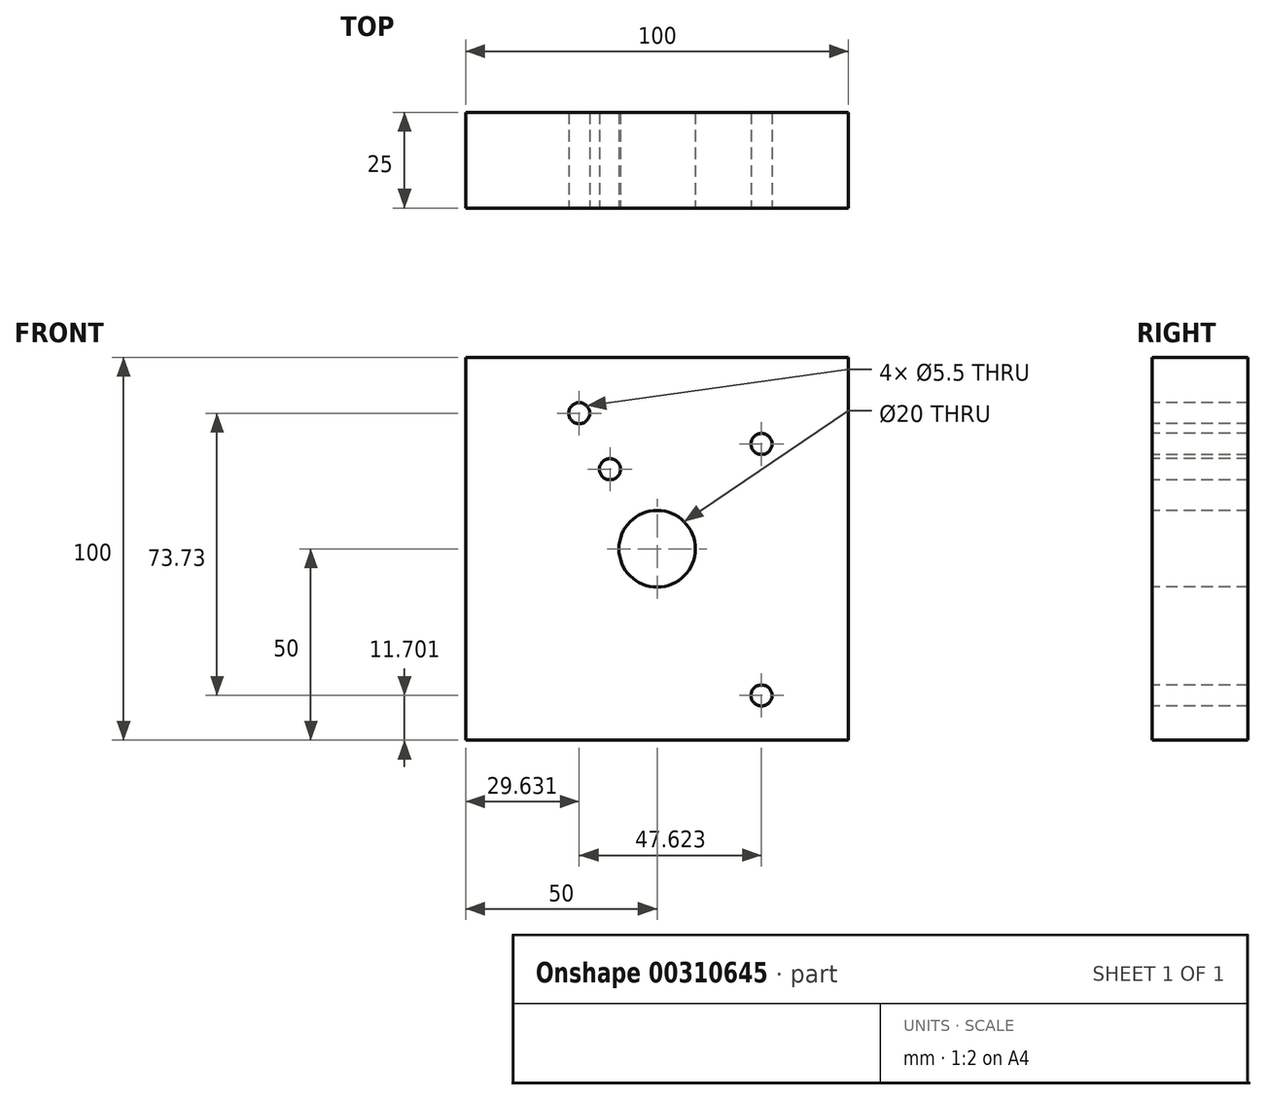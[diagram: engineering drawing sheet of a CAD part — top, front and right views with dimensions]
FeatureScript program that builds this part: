
annotation { "Feature Type Name" : "Feature", "Feature Type Description" : "" }
export const myFeature = defineFeature(function(context is Context, id is Id, definition is map)
    precondition{}
    {
        {
            var Q0;
            Q0=qCreatedBy(makeId("Front.planeOp"),FACE);
            var sketch = newSketch(context, id + "F0", { "sketchPlane" : qUnion([Q0])});
            skLineSegment(sketch, "E0.bottom", {"start": v(-50, 50) * mm, "end": v(50, 50) * mm});
            skLineSegment(sketch, "E0.top", {"start": v(-50, -50) * mm, "end": v(50, -50) * mm});
            skLineSegment(sketch, "E0.left", {"start": v(-50, 50) * mm, "end": v(-50, -50) * mm});
            skLineSegment(sketch, "E0.right", {"start": v(50, 50) * mm, "end": v(50, -50) * mm});
            skPoint(sketch, "E0.middle", {"position": v(0, 0) * mm});
            skSolve(sketch);
        }
        {
            var Q0;
            Q0=makeQuery(id+"F0.imprint","IMPRINT",FACE,{"disambiguationData":[TD([[makeQuery(id+"F0.imprint","IMPRINT",EDGE,{"derivedFrom":sQuery(id+"F0.wireOp",EDGE,"E0.bottom")}),-1.0]])]});
            extrude(context, id + "F1", {"entities" : qUnion([Q0]), "depth" : 25 * mm});
        }
        {
            var Q0;
            Q0=makeQuery(id+"F1.opExtrude","CAP_FACE",FACE,{"disambiguationData":[OSD([sQuery(id+"F0.wireOp",EDGE,"E0.bottom"),sQuery(id+"F0.wireOp",EDGE,"E0.top"),sQuery(id+"F0.wireOp",EDGE,"E0.left"),sQuery(id+"F0.wireOp",EDGE,"E0.right")])],"isStart":false});
            var sketch = newSketch(context, id + "F2", { "sketchPlane" : qUnion([Q0])});
            skCircle(sketch, "E1", {"center": v(0, 0) * mm, "radius": 8.1 * mm});
            skSolve(sketch);
        }
        {
            var Q0;
            Q0=sQuery(id+"F2.wireOp",VERTEX,"E1.center");
            var Q1;
            Q1=makeQuery(id+"F1.opExtrude","SWEPT_BODY",BODY,{"disambiguationData":[OSD([sQuery(id+"F0.wireOp",EDGE,"E0.bottom"),sQuery(id+"F0.wireOp",EDGE,"E0.top"),sQuery(id+"F0.wireOp",EDGE,"E0.left"),sQuery(id+"F0.wireOp",EDGE,"E0.right")])]});
            hole(context, id + "F3", {"style" : HoleStyle.SIMPLE, "endStyle" : HoleEndStyle.THROUGH, "holeDiameter" : 20 * mm, "tappedDepth" : 12 * mm, "tapClearance" : 3, "locations" : qUnion([Q0]), "scope" : qUnion([Q1])});
        }
        {
            var Q0;
            Q0=makeQuery(id+"F1.opExtrude","CAP_FACE",FACE,{"disambiguationData":[OSD([sQuery(id+"F0.wireOp",EDGE,"E0.bottom"),sQuery(id+"F0.wireOp",EDGE,"E0.top"),sQuery(id+"F0.wireOp",EDGE,"E0.left"),sQuery(id+"F0.wireOp",EDGE,"E0.right")])],"isStart":false});
            var sketch = newSketch(context, id + "F4", { "sketchPlane" : qUnion([Q0])});
            skLineSegment(sketch, "E2", {"start": v(0, 10) * mm, "end": v(0, 21.66) * mm});
            skLineSegment(sketch, "E3", {"start": v(0, 21.66) * mm, "end": v(13.2, 21.66) * mm});
            skLineSegment(sketch, "E4", {"start": v(13.2, 21.66) * mm, "end": v(13.2, 0) * mm});
            skLineSegment(sketch, "E5", {"start": v(13.2, 0) * mm, "end": v(13.2, -12.2) * mm});
            skLineSegment(sketch, "E6", {"start": v(13.2, -12.2) * mm, "end": v(-10.9, -12.2) * mm});
            skLineSegment(sketch, "E7", {"start": v(-10.9, -12.2) * mm, "end": v(-16.35, -12.2) * mm});
            skLineSegment(sketch, "E8", {"start": v(-16.35, -12.2) * mm, "end": v(-16.35, 27.4) * mm});
            skLineSegment(sketch, "E9", {"start": v(-16.35, 27.4) * mm, "end": v(18.07, 27.4) * mm});
            skLineSegment(sketch, "E10", {"start": v(18.07, 27.4) * mm, "end": v(18.07, 0) * mm});
            skLineSegment(sketch, "E11", {"start": v(18.07, 0) * mm, "end": v(18.07, -12.2) * mm});
            skLineSegment(sketch, "E12", {"start": v(18.07, -12.2) * mm, "end": v(18.07, -19.08) * mm});
            skLineSegment(sketch, "E13", {"start": v(18.07, -19.08) * mm, "end": v(0, -19.08) * mm});
            skLineSegment(sketch, "E14", {"start": v(0, -19.08) * mm, "end": v(-16.35, -19.08) * mm});
            skLineSegment(sketch, "E15", {"start": v(-16.35, -19.08) * mm, "end": v(-24.1, -19.08) * mm});
            skLineSegment(sketch, "E16", {"start": v(-24.1, -19.08) * mm, "end": v(-24.1, 32.27) * mm});
            skLineSegment(sketch, "E17", {"start": v(-24.1, 32.27) * mm, "end": v(23.24, 32.27) * mm});
            skLineSegment(sketch, "E18", {"start": v(23.24, 32.27) * mm, "end": v(23.24, 0) * mm});
            skLineSegment(sketch, "E19", {"start": v(23.24, 0) * mm, "end": v(23.24, -19.08) * mm});
            skLineSegment(sketch, "E20", {"start": v(23.24, -19.08) * mm, "end": v(23.24, -27.97) * mm});
            skLineSegment(sketch, "E21", {"start": v(23.24, -27.97) * mm, "end": v(-2.58, -27.97) * mm});
            skLineSegment(sketch, "E22", {"start": v(-2.58, -27.97) * mm, "end": v(-31.27, -27.97) * mm});
            skLineSegment(sketch, "E23", {"start": v(-31.27, -27.97) * mm, "end": v(-31.27, 40.88) * mm});
            skLineSegment(sketch, "E24", {"start": v(-31.27, 40.88) * mm, "end": v(8.73, 40.88) * mm});
            skLineSegment(sketch, "E25", {"start": v(8.73, 40.88) * mm, "end": v(34.14, 40.88) * mm});
            skLineSegment(sketch, "E26", {"start": v(34.14, 40.88) * mm, "end": v(34.14, 0) * mm});
            skLineSegment(sketch, "E27", {"start": v(34.14, 0) * mm, "end": v(34.14, -35.24) * mm});
            skLineSegment(sketch, "E28", {"start": v(34.14, -35.24) * mm, "end": v(34.14, -32.66) * mm});
            skLineSegment(sketch, "E29", {"start": v(34.14, -32.66) * mm, "end": v(34.14, -35.24) * mm});
            skLineSegment(sketch, "E30", {"start": v(34.14, -35.24) * mm, "end": v(-2.58, -35.24) * mm});
            skLineSegment(sketch, "E31", {"start": v(-2.58, -35.24) * mm, "end": v(-35.86, -35.24) * mm});
            skLineSegment(sketch, "E32", {"start": v(-35.86, -35.24) * mm, "end": v(-35.86, 15.54) * mm});
            skLineSegment(sketch, "E33", {"start": v(-35.86, 15.54) * mm, "end": v(-35.86, 41.93) * mm});
            skLineSegment(sketch, "E34", {"start": v(-35.86, 41.93) * mm, "end": v(40.45, 41.93) * mm});
            skLineSegment(sketch, "E35", {"start": v(40.45, 41.93) * mm, "end": v(40.45, -35.24) * mm});
            skLineSegment(sketch, "E36", {"start": v(40.45, -35.24) * mm, "end": v(40.45, -41.45) * mm});
            skLineSegment(sketch, "E37", {"start": v(40.45, -41.45) * mm, "end": v(-2.58, -41.45) * mm});
            skLineSegment(sketch, "E38", {"start": v(-2.58, -41.45) * mm, "end": v(-40.74, -41.45) * mm});
            skLineSegment(sketch, "E39", {"start": v(-40.74, -2.15) * mm, "end": v(-40.74, -41.45) * mm});
            skLineSegment(sketch, "E40", {"start": v(-40.74, 32.27) * mm, "end": v(-40.74, -2.15) * mm});
            skLineSegment(sketch, "E41", {"start": v(-40.74, 47.48) * mm, "end": v(-40.74, 32.27) * mm});
            skLineSegment(sketch, "E42", {"start": v(-40.74, 47.48) * mm, "end": v(0, 47.48) * mm});
            skLineSegment(sketch, "E43", {"start": v(0, 47.48) * mm, "end": v(40.45, 47.48) * mm});
            skLineSegment(sketch, "E44", {"start": v(40.45, 47.48) * mm, "end": v(46.48, 47.48) * mm});
            skLineSegment(sketch, "E45", {"start": v(46.48, 47.48) * mm, "end": v(46.48, 0) * mm});
            skLineSegment(sketch, "E46", {"start": v(46.48, 0) * mm, "end": v(46.48, -47) * mm});
            skLineSegment(sketch, "E47", {"start": v(46.48, -47) * mm, "end": v(13.2, -47) * mm});
            skLineSegment(sketch, "E48", {"start": v(13.2, -47) * mm, "end": v(-35.86, -47) * mm});
            skLineSegment(sketch, "E49", {"start": v(-35.86, -47) * mm, "end": v(-46.76, -47) * mm});
            skLineSegment(sketch, "E50", {"start": v(-46.76, -47) * mm, "end": v(-46.76, -2.15) * mm});
            skLineSegment(sketch, "E51", {"start": v(-46.76, -2.15) * mm, "end": v(-50, -2.15) * mm});
            skLineSegment(sketch, "E52.0", {"start": v(-46.76, 2.85) * mm, "end": v(-50, 2.85) * mm});
            skLineSegment(sketch, "E53.0", {"start": v(-43.76, -47) * mm, "end": v(-43.76, -4.83) * mm});
            skLineSegment(sketch, "E54.0", {"start": v(-28.27, 35.88) * mm, "end": v(34.14, 35.88) * mm});
            skSolve(sketch);
        }
        {
            var Q0;
            {var subQ1=makeQuery(id+"F1.opExtrude","CAP_EDGE",EDGE,{"disambiguationData":[OSD([sQuery(id+"F0.wireOp",EDGE,"E0.bottom")])],"isStart":false});Q0=makeQuery(id+"F4.imprint","IMPRINT",FACE,{"disambiguationData":[TD([[makeQuery(id+"F4.imprint","IMPRINT",EDGE,{"derivedFrom":subQ1}),-1.0]])]});}
            var sketch = newSketch(context, id + "F5", { "sketchPlane" : qUnion([Q0])});
            skCircle(sketch, "E55", {"center": v(27.25, 27.4) * mm, "radius": 3.17 * mm});
            skCircle(sketch, "E56", {"center": v(-20.37, 35.43) * mm, "radius": 3.09 * mm});
            skCircle(sketch, "E57", {"center": v(-12.34, 20.8) * mm, "radius": 3.45 * mm});
            skCircle(sketch, "E58", {"center": v(27.25, -38.3) * mm, "radius": 3.27 * mm});
            skSolve(sketch);
        }
        {
            var Q0;
            Q0=sQuery(id+"F5.wireOp",VERTEX,"E55.center");
            var Q1;
            Q1=sQuery(id+"F5.wireOp",VERTEX,"E57.center");
            var Q2;
            Q2=sQuery(id+"F5.wireOp",VERTEX,"E56.center");
            var Q3;
            Q3=sQuery(id+"F5.wireOp",VERTEX,"E58.center");
            var Q4;
            Q4=makeQuery(id+"F1.opExtrude","SWEPT_BODY",BODY,{"disambiguationData":[OSD([sQuery(id+"F0.wireOp",EDGE,"E0.bottom"),sQuery(id+"F0.wireOp",EDGE,"E0.top"),sQuery(id+"F0.wireOp",EDGE,"E0.left"),sQuery(id+"F0.wireOp",EDGE,"E0.right")])]});
            hole(context, id + "F6", {"style" : HoleStyle.SIMPLE, "endStyle" : HoleEndStyle.THROUGH, "standardTappedOrClearance" : lookupTablePath({ "standard" : "ISO", "fit" : "Normal", "size" : "M5", "type" : "Clearance" }), "standardBlindInLast" : lookupTablePath({ "fit" : "Standard", "standard" : "ISO", "size" : "M5", "type" : "Clearance" }), "holeDiameter" : 5.5 * mm, "tappedDepth" : 12 * mm, "tapClearance" : 3, "locations" : qUnion([Q0, Q1, Q2, Q3]), "scope" : qUnion([Q4])});
        }
    });
